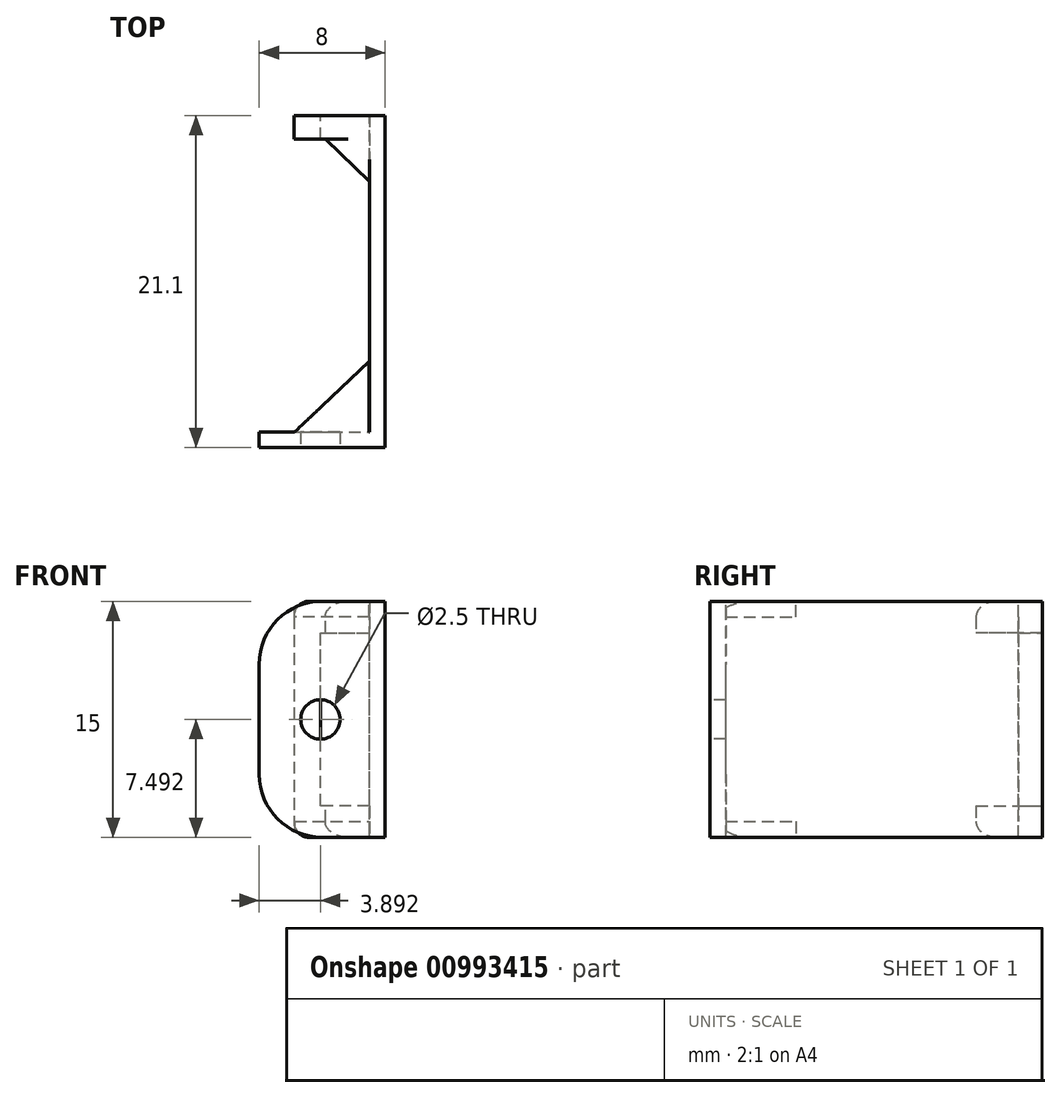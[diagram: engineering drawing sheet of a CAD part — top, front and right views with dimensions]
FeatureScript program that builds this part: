
annotation { "Feature Type Name" : "Feature", "Feature Type Description" : "" }
export const myFeature = defineFeature(function(context is Context, id is Id, definition is map)
    precondition{}
    {
        {
            var Q0;
            Q0=qCreatedBy(makeId("Top.planeOp"),FACE);
            var sketch = newSketch(context, id + "F0", { "sketchPlane" : qUnion([Q0])});
            skLineSegment(sketch, "E0", {"start": v(-8, 0) * mm, "end": v(0, 0) * mm});
            skLineSegment(sketch, "E1", {"start": v(0, 0) * mm, "end": v(0, 20.1) * mm});
            skSolve(sketch);
        }
        {
            var Q0;
            Q0=sQuery(id+"F0.wireOp",EDGE,"E1");
            var Q1;
            Q1=sQuery(id+"F0.wireOp",EDGE,"E0");
            extrude(context, id + "F1", {"bodyType" : ToolBodyType.SURFACE, "surfaceEntities" : qUnion([Q0, Q1]), "depth" : 15 * mm, "offsetDistance" : 25 * mm});
        }
        {
            var Q0;
            Q0=makeQuery(id+"F1.opExtrude","SWEPT_FACE",FACE,{"disambiguationData":[OSD([sQuery(id+"F0.wireOp",EDGE,"E1")])]});
            extrude(context, id + "F2", {"entities" : qUnion([Q0]), "oppositeDirection" : true, "depth" : 1 * mm, "offsetDistance" : 25 * mm});
        }
        {
            var Q0;
            Q0=makeQuery(id+"F1.opExtrude","SWEPT_FACE",FACE,{"disambiguationData":[OSD([sQuery(id+"F0.wireOp",EDGE,"E0")])]});
            extrude(context, id + "F3", {"entities" : qUnion([Q0]), "depth" : 1 * mm, "offsetDistance" : 25 * mm});
        }
        {
            var Q0;
            Q0=qCreatedBy(makeId("Top.planeOp"),FACE);
            var sketch = newSketch(context, id + "F4", { "sketchPlane" : qUnion([Q0])});
            skLineSegment(sketch, "E2", {"start": v(-1.01, 0) * mm, "end": v(-1.01, 4.46) * mm});
            skLineSegment(sketch, "E3", {"start": v(-1.01, 4.46) * mm, "end": v(-5.75, 0) * mm});
            skLineSegment(sketch, "E4", {"start": v(-5.75, 0) * mm, "end": v(-1.01, 0) * mm});
            skSolve(sketch);
        }
        {
            var Q0;
            Q0=qSketchRegion(id+"F4",true);
            extrude(context, id + "F5", {"entities" : qUnion([Q0]), "operationType" : NewBodyOperationType.ADD, "depth" : 1 * mm, "offsetDistance" : 25 * mm});
        }
        {
            var Q0;
            {var subQ0=sQuery(id+"F0.wireOp",EDGE,"E0");Q0=makeQuery(id+"F3.opExtrude","SWEPT_FACE",FACE,{"disambiguationData":[OSD([subQ0]),TDD([makeQuery(id+"F1.opExtrude","CAP_EDGE",EDGE,{"disambiguationData":[OSD([subQ0])],"isStart":false})])]});}
            var sketch = newSketch(context, id + "F6", { "sketchPlane" : qUnion([Q0])});
            skLineSegment(sketch, "E5", {"start": v(-1.02, 0) * mm, "end": v(-1.02, 4.46) * mm});
            skLineSegment(sketch, "E6", {"start": v(-1.02, 4.46) * mm, "end": v(-5.75, 0) * mm});
            skLineSegment(sketch, "E7", {"start": v(-5.75, 0) * mm, "end": v(-1.02, 0) * mm});
            skSolve(sketch);
        }
        {
            var Q0;
            Q0=qSketchRegion(id+"F6",true);
            extrude(context, id + "F7", {"entities" : qUnion([Q0]), "oppositeDirection" : true, "depth" : 1 * mm, "offsetDistance" : 25 * mm});
        }
        {
            var Q0;
            Q0=makeQuery(id+"FDkcNweglCsyA08_3.boolean.opBoolean","SPLIT",FACE,{"disambiguationData":[TD([makeQuery(id+"FDkcNweglCsyA08_3.opExtrude","SWEPT_FACE",FACE,{"disambiguationData":[OSD([sQuery(id+"FIDp8no4e9qmnIs_1.wireOp",EDGE,"D3e9rV2e-k7Sn-KW6I-SL6g-XI2bMzRzFWo7.bottom")])]})])],"derivedFrom":makeQuery(id+"F2.opExtrude","SWEPT_FACE",FACE,{"disambiguationData":[OSD([sQuery(id+"F0.wireOp",VERTEX,"E1.end")])]})});
            var sketch = newSketch(context, id + "F8", { "sketchPlane" : qUnion([Q0])});
            skLineSegment(sketch, "E8", {"start": v(0, 15) * mm, "end": v(5.8, 15) * mm});
            skLineSegment(sketch, "E9", {"start": v(5.8, 15) * mm, "end": v(5.8, 0) * mm});
            skLineSegment(sketch, "E10", {"start": v(5.8, 0) * mm, "end": v(0, 0) * mm});
            skLineSegment(sketch, "E11", {"start": v(0, 0) * mm, "end": v(0, 2) * mm});
            skLineSegment(sketch, "E12", {"start": v(0, 2) * mm, "end": v(4.1, 2) * mm});
            skLineSegment(sketch, "E13", {"start": v(4.1, 2) * mm, "end": v(4.1, 13) * mm});
            skLineSegment(sketch, "E14", {"start": v(4.1, 13) * mm, "end": v(0, 13) * mm});
            skLineSegment(sketch, "E15", {"start": v(0, 13) * mm, "end": v(0, 15) * mm});
            skSolve(sketch);
        }
        {
            var Q0;
            Q0 = qSketchRegion(id + "F8", true);
            extrude(context, id + "F9", {"entities" : qUnion([Q0]), "operationType" : NewBodyOperationType.ADD, "oppositeDirection" : true, "depth" : 1.5 * mm, "offsetDistance" : 25 * mm});
        }
        {
            var Q0;
            Q0=makeQuery(id+"F7.opExtrude","SWEPT_BODY",BODY,{"disambiguationData":[OSD([sQuery(id+"F6.wireOp",EDGE,"E5"),sQuery(id+"F6.wireOp",EDGE,"E6"),sQuery(id+"F6.wireOp",EDGE,"E7")])]});
            var Q1;
            Q1=makeQuery(id+"F3.opExtrude","SWEPT_BODY",BODY,{"disambiguationData":[OSD([sQuery(id+"F0.wireOp",EDGE,"E0")])]});
            var Q2;
            Q2=makeQuery(id+"F2.opExtrude","SWEPT_BODY",BODY,{"disambiguationData":[OSD([sQuery(id+"F0.wireOp",EDGE,"E1")])]});
            booleanBodies(context, id + "F10", {"operationType" : BooleanOperationType.UNION, "tools" : qUnion([Q0, Q1, Q2])});
        }
        {
            var Q0;
            {var subQ0=sQuery(id+"F0.wireOp",VERTEX,"E0.start");Q0=makeQuery(id+"F3.opExtrude","SWEPT_EDGE",EDGE,{"disambiguationData":[OSD([subQ0]),TDD([makeQuery(id+"F1.opExtrude","CAP_VERTEX",VERTEX,{"disambiguationData":[OSD([subQ0])],"isStart":true})])]});}
            var Q1;
            {var subQ0=sQuery(id+"F0.wireOp",VERTEX,"E0.start");Q1=makeQuery(id+"F3.opExtrude","SWEPT_EDGE",EDGE,{"disambiguationData":[OSD([subQ0]),TDD([makeQuery(id+"F1.opExtrude","CAP_VERTEX",VERTEX,{"disambiguationData":[OSD([subQ0])],"isStart":false})])]});}
            fillet(context, id + "F11", {"entities" : qUnion([Q0, Q1]), "radius" : 4 * mm, "tangentPropagation" : true, "allowEdgeOverflow" : false});
        }
        {
            var Q0;
            Q0=makeQuery(id+"F9.opExtrude","SWEPT_EDGE",EDGE,{"disambiguationData":[OSD([sQuery(id+"F8.wireOp",EDGE,"E9"),sQuery(id+"F8.wireOp",EDGE,"E10")])]});
            var Q1;
            Q1=makeQuery(id+"F9.opExtrude","SWEPT_EDGE",EDGE,{"disambiguationData":[OSD([sQuery(id+"F8.wireOp",EDGE,"E8"),sQuery(id+"F8.wireOp",EDGE,"E9")])]});
            fillet(context, id + "F12", {"entities" : qUnion([Q0, Q1]), "radius" : 1 * mm, "tangentPropagation" : true, "allowEdgeOverflow" : false});
        }
        {
            var Q0;
            Q0=makeQuery(id+"F9.boolean.opBoolean","INTERSECT",EDGE,{"disambiguationData":[OD(1.0)],"derivedFrom":[makeQuery(id+"F2.opExtrude","CAP_FACE",FACE,{"disambiguationData":[OSD([sQuery(id+"F0.wireOp",EDGE,"E1")])],"isStart":false}),makeQuery(id+"F9.opExtrude","CAP_FACE",FACE,{"disambiguationData":[OSD([sQuery(id+"F8.wireOp",EDGE,"E8"),sQuery(id+"F8.wireOp",EDGE,"E9"),sQuery(id+"F8.wireOp",EDGE,"E10"),sQuery(id+"F8.wireOp",EDGE,"E11"),sQuery(id+"F8.wireOp",EDGE,"E12"),sQuery(id+"F8.wireOp",EDGE,"E13"),sQuery(id+"F8.wireOp",EDGE,"E14"),sQuery(id+"F8.wireOp",EDGE,"E15")])],"isStart":false})]});
            var Q1;
            Q1=makeQuery(id+"F9.boolean.opBoolean","INTERSECT",EDGE,{"disambiguationData":[OD(0.0)],"derivedFrom":[makeQuery(id+"F2.opExtrude","CAP_FACE",FACE,{"disambiguationData":[OSD([sQuery(id+"F0.wireOp",EDGE,"E1")])],"isStart":false}),makeQuery(id+"F9.opExtrude","CAP_FACE",FACE,{"disambiguationData":[OSD([sQuery(id+"F8.wireOp",EDGE,"E8"),sQuery(id+"F8.wireOp",EDGE,"E9"),sQuery(id+"F8.wireOp",EDGE,"E10"),sQuery(id+"F8.wireOp",EDGE,"E11"),sQuery(id+"F8.wireOp",EDGE,"E12"),sQuery(id+"F8.wireOp",EDGE,"E13"),sQuery(id+"F8.wireOp",EDGE,"E14"),sQuery(id+"F8.wireOp",EDGE,"E15")])],"isStart":false})]});
            chamfer(context, id + "F13", {"entities" : qUnion([Q0, Q1]), "chamferType" : ChamferType.OFFSET_ANGLE, "width" : 2.8 * mm, "oppositeDirection" : false, "angle" : 44 * degree, "tangentPropagation" : true});
        }
        {
            var Q0;
            {var subQ0=sQuery(id+"F8.wireOp",EDGE,"E8");var subQ1=sQuery(id+"F0.wireOp",EDGE,"E1");var subQ2=sQuery(id+"F0.wireOp",EDGE,"E0");Q0=makeQuery(id+"F13.opChamfer","BLEND_EDGE",EDGE,{"blendedFrom":[makeQuery(id+"F9.boolean.opBoolean","INTERSECT",EDGE,{"disambiguationData":[OD(1.0)],"derivedFrom":[makeQuery(id+"F2.opExtrude","CAP_FACE",FACE,{"disambiguationData":[OSD([subQ1])],"isStart":false}),makeQuery(id+"F9.opExtrude","CAP_FACE",FACE,{"disambiguationData":[OSD([subQ0,sQuery(id+"F8.wireOp",EDGE,"E9"),sQuery(id+"F8.wireOp",EDGE,"E10"),sQuery(id+"F8.wireOp",EDGE,"E11"),sQuery(id+"F8.wireOp",EDGE,"E12"),sQuery(id+"F8.wireOp",EDGE,"E13"),sQuery(id+"F8.wireOp",EDGE,"E14"),sQuery(id+"F8.wireOp",EDGE,"E15")])],"isStart":false})]}),makeQuery(id+"F10.opBoolean","MERGE",FACE,{"derivedFrom":[makeQuery(id+"F3.opExtrude","SWEPT_FACE",FACE,{"disambiguationData":[OSD([subQ2]),TDD([makeQuery(id+"F1.opExtrude","CAP_EDGE",EDGE,{"disambiguationData":[OSD([subQ2])],"isStart":false})])]}),makeQuery(id+"F7.opExtrude","CAP_FACE",FACE,{"disambiguationData":[OSD([sQuery(id+"F6.wireOp",EDGE,"E5"),sQuery(id+"F6.wireOp",EDGE,"E6"),sQuery(id+"F6.wireOp",EDGE,"E7")])],"isStart":true}),makeQuery(id+"F9.boolean.opBoolean","MERGE",FACE,{"derivedFrom":[makeQuery(id+"F2.opExtrude","SWEPT_FACE",FACE,{"disambiguationData":[OSD([subQ1]),TDD([makeQuery(id+"F1.opExtrude","CAP_EDGE",EDGE,{"disambiguationData":[OSD([subQ1])],"isStart":false})])]}),makeQuery(id+"F9.opExtrude","SWEPT_FACE",FACE,{"disambiguationData":[OSD([subQ0])]})]})]})],"blendedInto":[makeQuery(id+"F10.opBoolean","MERGE",FACE,{"derivedFrom":[makeQuery(id+"F3.opExtrude","SWEPT_FACE",FACE,{"disambiguationData":[OSD([subQ2]),TDD([makeQuery(id+"F1.opExtrude","CAP_EDGE",EDGE,{"disambiguationData":[OSD([subQ2])],"isStart":false})])]}),makeQuery(id+"F7.opExtrude","CAP_FACE",FACE,{"disambiguationData":[OSD([sQuery(id+"F6.wireOp",EDGE,"E5"),sQuery(id+"F6.wireOp",EDGE,"E6"),sQuery(id+"F6.wireOp",EDGE,"E7")])],"isStart":true}),makeQuery(id+"F9.boolean.opBoolean","MERGE",FACE,{"derivedFrom":[makeQuery(id+"F2.opExtrude","SWEPT_FACE",FACE,{"disambiguationData":[OSD([subQ1]),TDD([makeQuery(id+"F1.opExtrude","CAP_EDGE",EDGE,{"disambiguationData":[OSD([subQ1])],"isStart":false})])]}),makeQuery(id+"F9.opExtrude","SWEPT_FACE",FACE,{"disambiguationData":[OSD([subQ0])]})]})]})]});}
            var Q1;
            {var subQ0=sQuery(id+"F8.wireOp",EDGE,"E10");var subQ1=sQuery(id+"F0.wireOp",EDGE,"E1");var subQ2=sQuery(id+"F0.wireOp",EDGE,"E0");Q1=makeQuery(id+"F13.opChamfer","BLEND_EDGE",EDGE,{"blendedFrom":[makeQuery(id+"F9.boolean.opBoolean","INTERSECT",EDGE,{"disambiguationData":[OD(0.0)],"derivedFrom":[makeQuery(id+"F2.opExtrude","CAP_FACE",FACE,{"disambiguationData":[OSD([subQ1])],"isStart":false}),makeQuery(id+"F9.opExtrude","CAP_FACE",FACE,{"disambiguationData":[OSD([sQuery(id+"F8.wireOp",EDGE,"E8"),sQuery(id+"F8.wireOp",EDGE,"E9"),subQ0,sQuery(id+"F8.wireOp",EDGE,"E11"),sQuery(id+"F8.wireOp",EDGE,"E12"),sQuery(id+"F8.wireOp",EDGE,"E13"),sQuery(id+"F8.wireOp",EDGE,"E14"),sQuery(id+"F8.wireOp",EDGE,"E15")])],"isStart":false})]}),makeQuery(id+"F10.opBoolean","MERGE",FACE,{"derivedFrom":[makeQuery(id+"F5.boolean.opBoolean","MERGE",FACE,{"derivedFrom":[makeQuery(id+"F3.opExtrude","SWEPT_FACE",FACE,{"disambiguationData":[OSD([subQ2]),TDD([makeQuery(id+"F1.opExtrude","CAP_EDGE",EDGE,{"disambiguationData":[OSD([subQ2])],"isStart":true})])]}),makeQuery(id+"F5.opExtrude","CAP_FACE",FACE,{"disambiguationData":[OSD([sQuery(id+"F4.wireOp",EDGE,"E2"),sQuery(id+"F4.wireOp",EDGE,"E3"),sQuery(id+"F4.wireOp",EDGE,"E4")])],"isStart":true})]}),makeQuery(id+"F9.boolean.opBoolean","MERGE",FACE,{"derivedFrom":[makeQuery(id+"F2.opExtrude","SWEPT_FACE",FACE,{"disambiguationData":[OSD([subQ1]),TDD([makeQuery(id+"F1.opExtrude","CAP_EDGE",EDGE,{"disambiguationData":[OSD([subQ1])],"isStart":true})])]}),makeQuery(id+"F9.opExtrude","SWEPT_FACE",FACE,{"disambiguationData":[OSD([subQ0])]})]})]})],"blendedInto":[makeQuery(id+"F10.opBoolean","MERGE",FACE,{"derivedFrom":[makeQuery(id+"F5.boolean.opBoolean","MERGE",FACE,{"derivedFrom":[makeQuery(id+"F3.opExtrude","SWEPT_FACE",FACE,{"disambiguationData":[OSD([subQ2]),TDD([makeQuery(id+"F1.opExtrude","CAP_EDGE",EDGE,{"disambiguationData":[OSD([subQ2])],"isStart":true})])]}),makeQuery(id+"F5.opExtrude","CAP_FACE",FACE,{"disambiguationData":[OSD([sQuery(id+"F4.wireOp",EDGE,"E2"),sQuery(id+"F4.wireOp",EDGE,"E3"),sQuery(id+"F4.wireOp",EDGE,"E4")])],"isStart":true})]}),makeQuery(id+"F9.boolean.opBoolean","MERGE",FACE,{"derivedFrom":[makeQuery(id+"F2.opExtrude","SWEPT_FACE",FACE,{"disambiguationData":[OSD([subQ1]),TDD([makeQuery(id+"F1.opExtrude","CAP_EDGE",EDGE,{"disambiguationData":[OSD([subQ1])],"isStart":true})])]}),makeQuery(id+"F9.opExtrude","SWEPT_FACE",FACE,{"disambiguationData":[OSD([subQ0])]})]})]})]});}
            fillet(context, id + "F14", {"entities" : qUnion([Q0, Q1]), "radius" : 1 * mm, "tangentPropagation" : true, "allowEdgeOverflow" : false});
        }
        {
            var Q0;
            Q0=makeQuery(id+"F3.opExtrude","CAP_FACE",FACE,{"disambiguationData":[OSD([sQuery(id+"F0.wireOp",EDGE,"E0")])],"isStart":false});
            var sketch = newSketch(context, id + "F15", { "sketchPlane" : qUnion([Q0])});
            skPoint(sketch, "E16", {"position": v(-4.1, 7.5) * mm});
            skSolve(sketch);
        }
        {
            var Q0;
            Q0=sQuery(id+"F15.wireOp",VERTEX,"E16");
            var Q1;
            Q1=makeQuery(id+"F7.opExtrude","SWEPT_BODY",BODY,{"disambiguationData":[OSD([sQuery(id+"F6.wireOp",EDGE,"E5"),sQuery(id+"F6.wireOp",EDGE,"E6"),sQuery(id+"F6.wireOp",EDGE,"E7")])]});
            hole(context, id + "F16", {"style" : HoleStyle.SIMPLE, "endStyle" : HoleEndStyle.BLIND, "holeDiameter" : 2.5 * mm, "majorDiameter" : 5 * mm, "holeDepth" : 3 * mm, "isTappedThrough" : true, "tappedDepth" : 12 * mm, "tapClearance" : 3, "locations" : qUnion([Q0]), "scope" : qUnion([Q1])});
        }
    });
